# Revit family: ASSA_ABLOY_DockLeveler_DL6120TA
name_source: partatom
category: Generic Models
units: mm (PartAtom-declared; Revit-internal decimal feet)

## family parameters
Always vertical = Yes
Can host rebar = No
Cut with Voids When Loaded = No
Part Type = Normal
Room Calculation Point = No
Round Connector Dimension = Use Diameter
Shared = No
Work Plane-Based = No

## types (3) — shared parameters
DL6120TA_LipErgoSteelLL345 = DL6120TA_LevelerTop : DL6120TA_LipErgoSteelLL345
DL6120TA_LipSteelLL1000 = DL6120TA_LevelerTop : DL6120TA_LipSteelLL1000
DL6120TA_LipSteelLL500 = DL6120TA_LevelerTop : DL6120TA_LipSteelLL500
Description = Docking Leveler
Manufacturer = ASSA ABLOY
Model = DL6120TA

## per-type parameters (varying)
| type | LipType | URL | Version |
| DL6120TA_LipSteelLL500 | DL6120TA_LevelerTop : DL6120TA_LipSteelLL500 |  | 0 |
| DL6120TA_LipErgoSteelLL345 | DL6120TA_LevelerTop : DL6120TA_LipErgoSteelLL345 |  | 0 |
| DL6120TA_LipSteelLL1000 | DL6120TA_LevelerTop : DL6120TA_LipSteelLL1000 | https://www.assaabloyentrance.com | 2 |

## geometry (parser evidence)
native form markers: Sweep x6
no freeform markers — native parametric forms only
